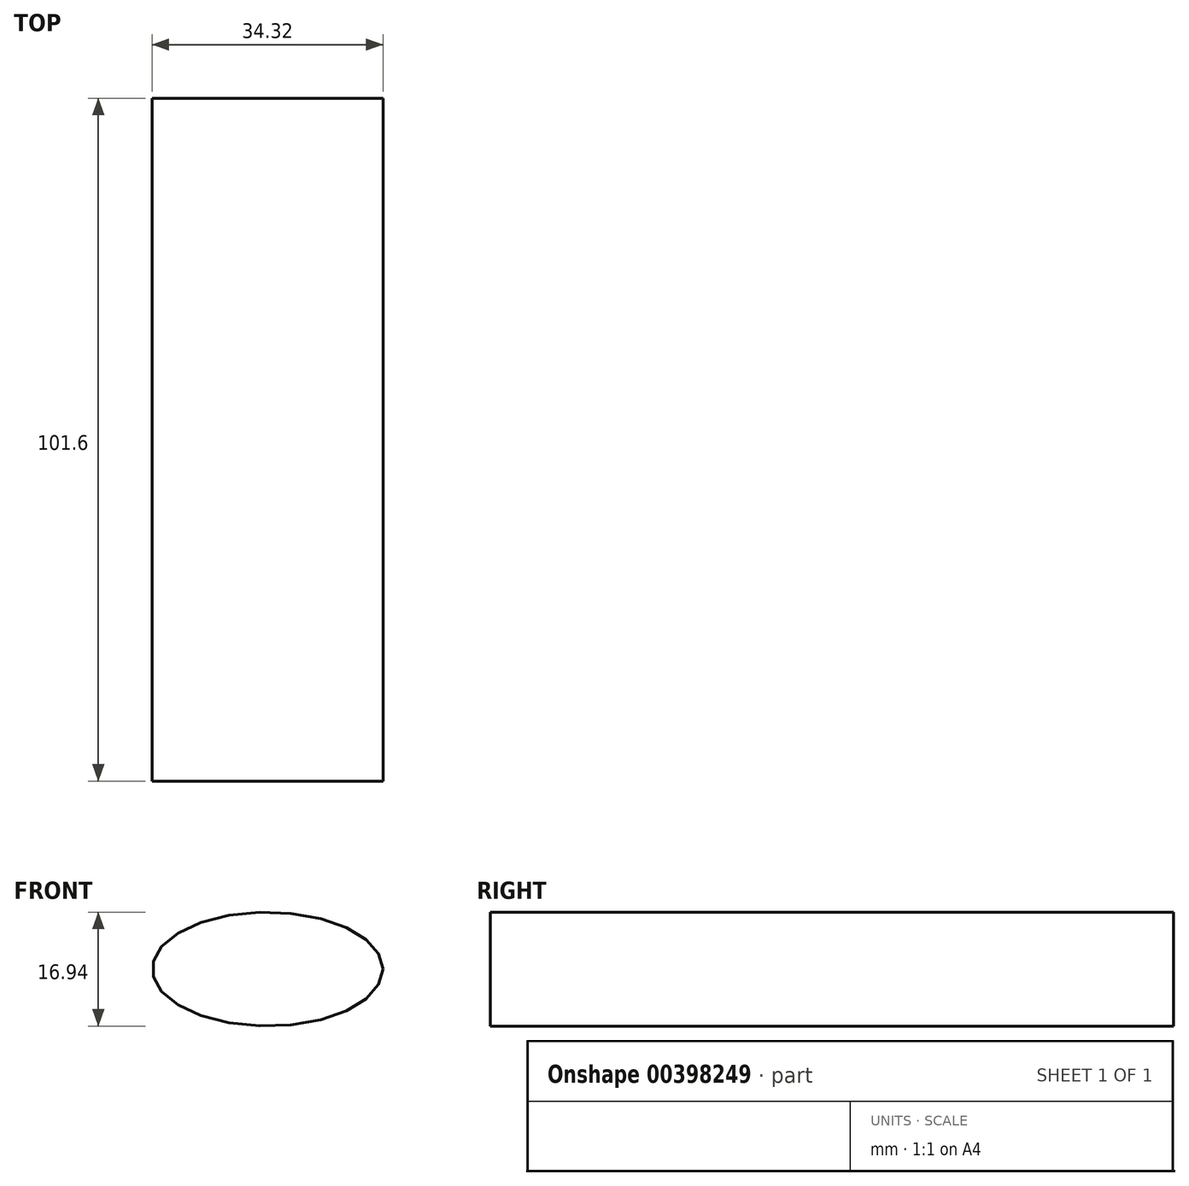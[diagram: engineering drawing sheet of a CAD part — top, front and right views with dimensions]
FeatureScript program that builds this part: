
annotation { "Feature Type Name" : "Feature", "Feature Type Description" : "" }
export const myFeature = defineFeature(function(context is Context, id is Id, definition is map)
    precondition{}
    {
        {
            var Q0;
            Q0=qCreatedBy(makeId("Front.planeOp"),FACE);
            var sketch = newSketch(context, id + "F0", { "sketchPlane" : qUnion([Q0])});
            skEllipse(sketch, "E0", {"center": v(0, 0) * mm, "majorRadius": 17.16 * mm, "minorRadius": 8.47 * mm, "majorAxis": v(1, 0)});
            skSolve(sketch);
        }
        {
            var Q0;
            Q0=makeQuery(id+"F0.imprint","IMPRINT",FACE,{"disambiguationData":[TD([[makeQuery(id+"F0.imprint","IMPRINT",EDGE,{"derivedFrom":sQuery(id+"F0.wireOp",EDGE,"E0")}),1.0]])]});
            extrude(context, id + "F1", {"entities" : qUnion([Q0]), "depth" : 101.6 * mm});
        }
    });
